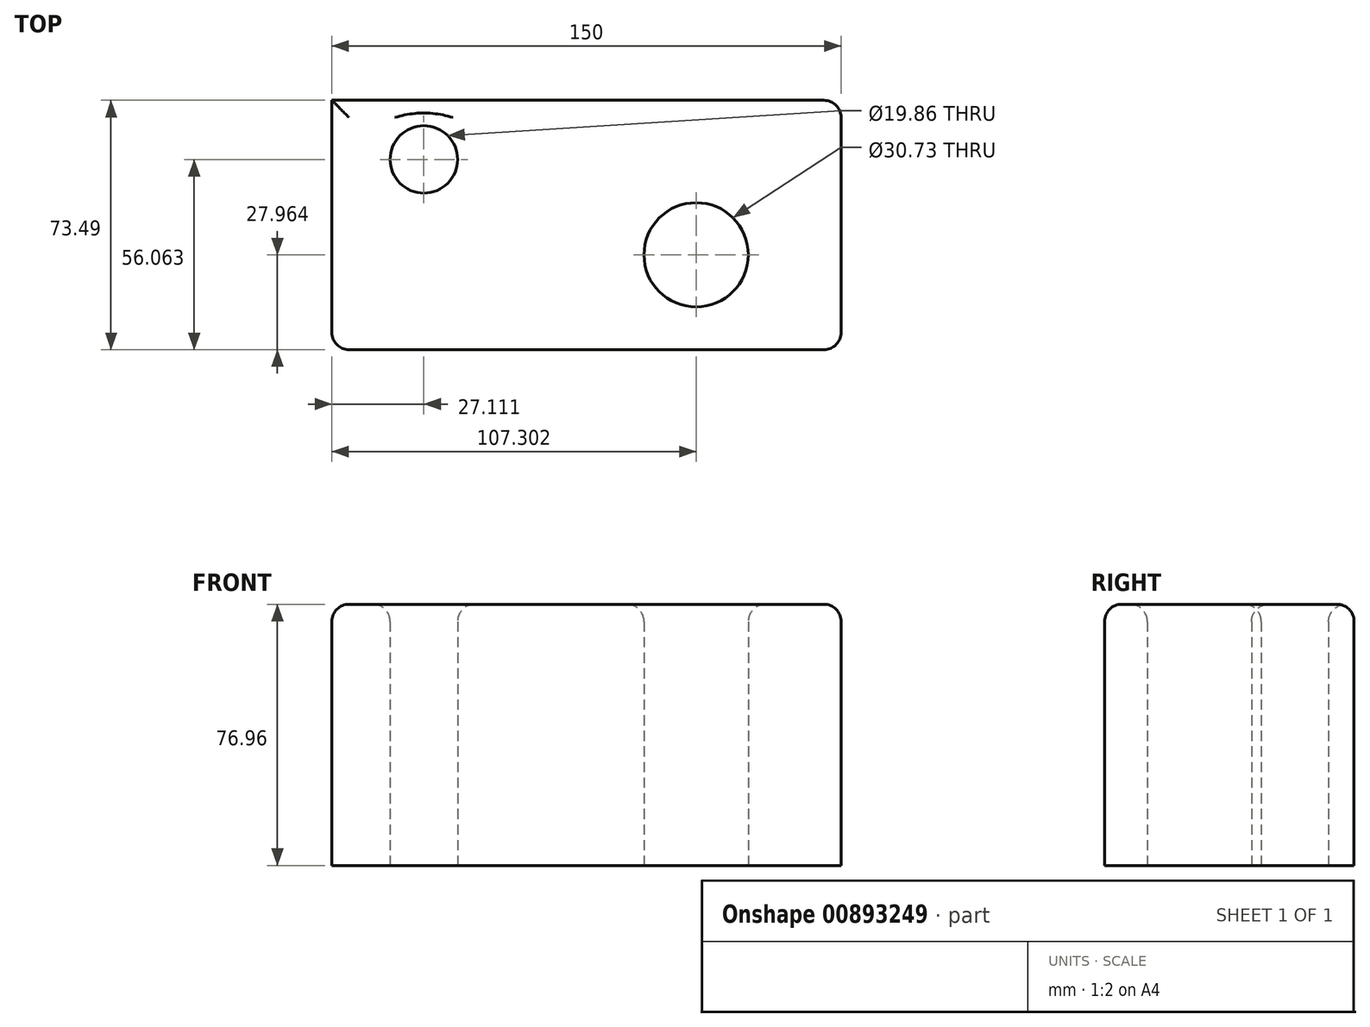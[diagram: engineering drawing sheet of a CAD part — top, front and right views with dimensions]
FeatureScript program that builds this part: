
annotation { "Feature Type Name" : "Feature", "Feature Type Description" : "" }
export const myFeature = defineFeature(function(context is Context, id is Id, definition is map)
    precondition{}
    {
        {
            var Q0;
            Q0=qCreatedBy(makeId("Top.planeOp"),FACE);
            var sketch = newSketch(context, id + "F0", { "sketchPlane" : qUnion([Q0])});
            skLineSegment(sketch, "E0.bottom", {"start": v(94.2, -70.87) * mm, "end": v(-55.8, -70.87) * mm});
            skLineSegment(sketch, "E0.top", {"start": v(94.2, 2.62) * mm, "end": v(-55.8, 2.62) * mm});
            skLineSegment(sketch, "E0.left", {"start": v(94.2, -70.87) * mm, "end": v(94.2, 2.62) * mm});
            skLineSegment(sketch, "E0.right", {"start": v(-55.8, -70.87) * mm, "end": v(-55.8, 2.62) * mm});
            skCircle(sketch, "E1", {"center": v(-28.69, -14.8) * mm, "radius": 9.93 * mm});
            skCircle(sketch, "E2", {"center": v(51.5, -42.9) * mm, "radius": 15.37 * mm});
            skSolve(sketch);
        }
        {
            var Q0;
            Q0=makeQuery(id+"F0.imprint","IMPRINT",FACE,{"disambiguationData":[TD([[makeQuery(id+"F0.imprint","IMPRINT",EDGE,{"derivedFrom":sQuery(id+"F0.wireOp",EDGE,"E0.bottom")}),-1.0]])]});
            extrude(context, id + "F1", {"entities" : qUnion([Q0]), "depth" : 76.96 * mm, "offsetDistance" : 25.4 * mm});
        }
        {
            var Q0;
            Q0=makeQuery(id+"F1.opExtrude","CAP_EDGE",EDGE,{"disambiguationData":[OSD([sQuery(id+"F0.wireOp",EDGE,"E2")])],"isStart":false});
            var Q1;
            Q1=makeQuery(id+"F1.opExtrude","CAP_EDGE",EDGE,{"disambiguationData":[OSD([sQuery(id+"F0.wireOp",EDGE,"E1")])],"isStart":false});
            var Q2;
            Q2=makeQuery(id+"F1.opExtrude","CAP_EDGE",EDGE,{"disambiguationData":[OSD([sQuery(id+"F0.wireOp",EDGE,"E0.bottom")])],"isStart":false});
            var Q3;
            Q3=makeQuery(id+"F1.opExtrude","CAP_EDGE",EDGE,{"disambiguationData":[OSD([sQuery(id+"F0.wireOp",EDGE,"E0.left")])],"isStart":false});
            var Q4;
            Q4=makeQuery(id+"F1.opExtrude","CAP_EDGE",EDGE,{"disambiguationData":[OSD([sQuery(id+"F0.wireOp",EDGE,"E0.top")])],"isStart":false});
            var Q5;
            Q5=makeQuery(id+"F1.opExtrude","CAP_EDGE",EDGE,{"disambiguationData":[OSD([sQuery(id+"F0.wireOp",EDGE,"E0.right")])],"isStart":false});
            var Q6;
            Q6=makeQuery(id+"F1.opExtrude","SWEPT_EDGE",EDGE,{"disambiguationData":[OSD([sQuery(id+"F0.wireOp",EDGE,"E0.bottom"),sQuery(id+"F0.wireOp",EDGE,"E0.left")])]});
            var Q7;
            Q7=makeQuery(id+"F1.opExtrude","SWEPT_EDGE",EDGE,{"disambiguationData":[OSD([sQuery(id+"F0.wireOp",EDGE,"E0.top"),sQuery(id+"F0.wireOp",EDGE,"E0.left")])]});
            var Q8;
            Q8=makeQuery(id+"F1.opExtrude","SWEPT_EDGE",EDGE,{"disambiguationData":[OSD([sQuery(id+"F0.wireOp",EDGE,"E0.bottom"),sQuery(id+"F0.wireOp",EDGE,"E0.right")])]});
            fillet(context, id + "F2", {"entities" : qUnion([Q0, Q1, Q2, Q3, Q4, Q5, Q6, Q7, Q8]), "radius" : 5.08 * mm, "tangentPropagation" : true, "allowEdgeOverflow" : false});
        }
    });
